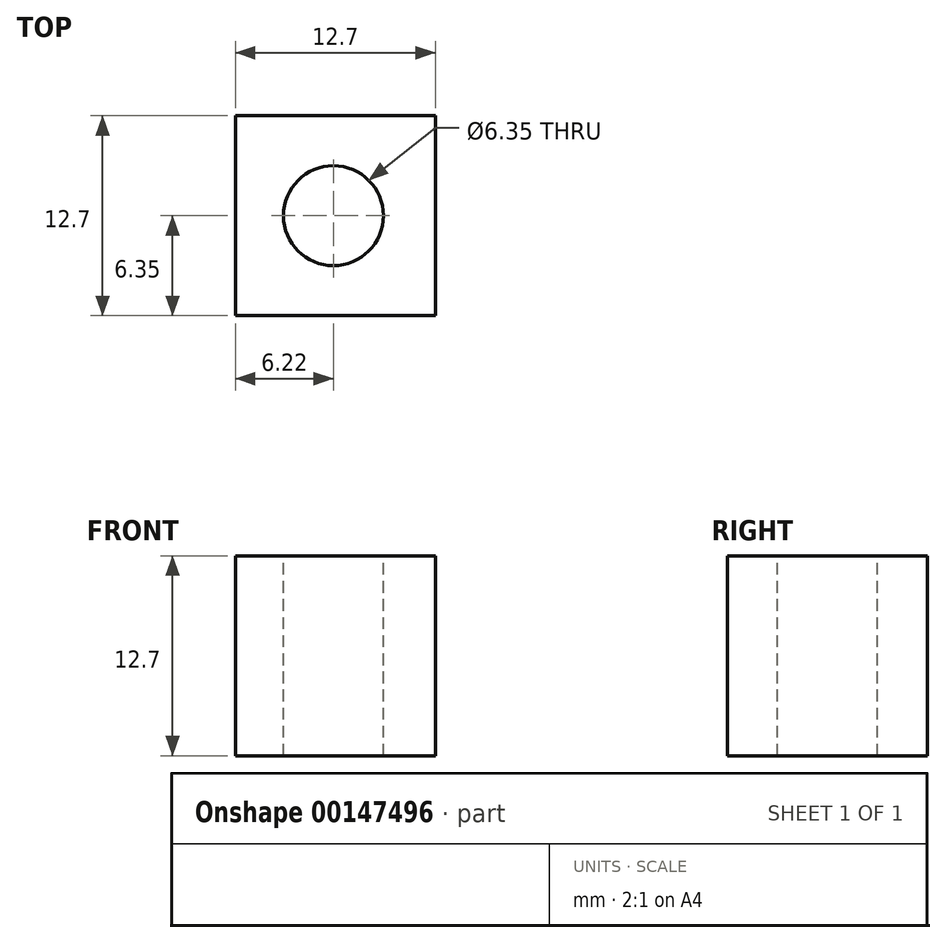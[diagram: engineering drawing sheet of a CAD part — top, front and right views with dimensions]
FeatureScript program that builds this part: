
annotation { "Feature Type Name" : "Feature", "Feature Type Description" : "" }
export const myFeature = defineFeature(function(context is Context, id is Id, definition is map)
    precondition{}
    {
        {
            var Q0;
            Q0=qCreatedBy(makeId("Front.planeOp"),FACE);
            var sketch = newSketch(context, id + "F0", { "sketchPlane" : qUnion([Q0])});
            skLineSegment(sketch, "E0.bottom", {"start": v(-6.22, 3.72) * mm, "end": v(6.48, 3.72) * mm});
            skLineSegment(sketch, "E0.top", {"start": v(-6.22, -8.98) * mm, "end": v(6.48, -8.98) * mm});
            skLineSegment(sketch, "E0.left", {"start": v(-6.22, 3.72) * mm, "end": v(-6.22, -8.98) * mm});
            skLineSegment(sketch, "E0.right", {"start": v(6.48, 3.72) * mm, "end": v(6.48, -8.98) * mm});
            skSolve(sketch);
        }
        {
            var Q0;
            Q0=makeQuery(id+"F0.imprint","IMPRINT",FACE,{"disambiguationData":[TD([[makeQuery(id+"F0.imprint","IMPRINT",EDGE,{"derivedFrom":sQuery(id+"F0.wireOp",EDGE,"E0.bottom")}),-1.0]])]});
            extrude(context, id + "F1", {"entities" : qUnion([Q0]), "depth" : 12.7 * mm});
        }
        {
            var Q0;
            Q0=makeQuery(id+"F1.opExtrude","SWEPT_FACE",FACE,{"disambiguationData":[OSD([sQuery(id+"F0.wireOp",EDGE,"E0.bottom")])]});
            var sketch = newSketch(context, id + "F2", { "sketchPlane" : qUnion([Q0])});
            skCircle(sketch, "E1", {"center": v(0, -6.35) * mm, "radius": 3.18 * mm});
            skPoint(sketch, "E1.centerSnap0", {"position": v(-6.22, -6.35) * mm});
            skSolve(sketch);
        }
        {
            var Q0;
            Q0=makeQuery(id+"F2.imprint","IMPRINT",FACE,{"disambiguationData":[TD([[makeQuery(id+"F2.imprint","IMPRINT",EDGE,{"derivedFrom":sQuery(id+"F2.wireOp",EDGE,"E1")}),1.0]])]});
            extrude(context, id + "F3", {"entities" : qUnion([Q0]), "operationType" : NewBodyOperationType.REMOVE, "oppositeDirection" : true, "depth" : 15.24 * mm});
        }
    });
